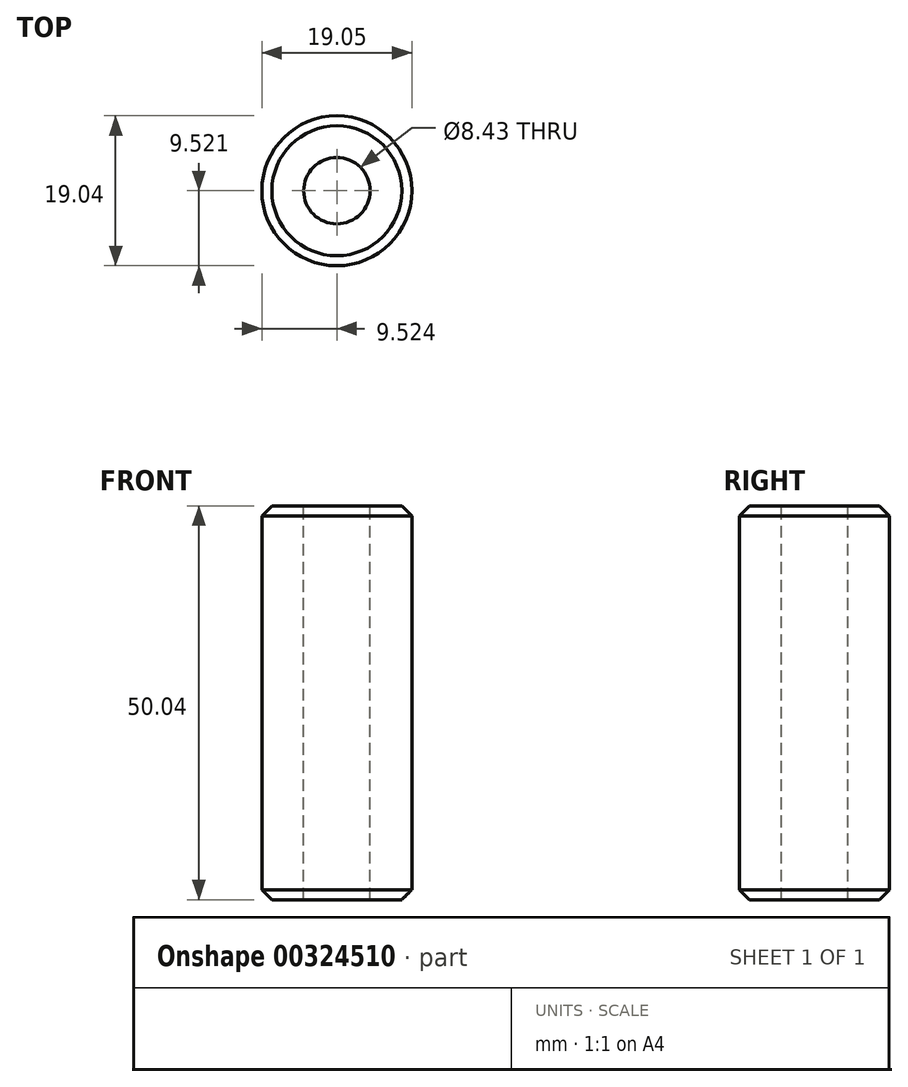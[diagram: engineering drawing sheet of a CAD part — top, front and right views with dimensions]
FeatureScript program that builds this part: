
annotation { "Feature Type Name" : "Feature", "Feature Type Description" : "" }
export const myFeature = defineFeature(function(context is Context, id is Id, definition is map)
    precondition{}
    {
        {
            var Q0;
            Q0=qCreatedBy(makeId("Top.planeOp"),FACE);
            var sketch = newSketch(context, id + "F0", { "sketchPlane" : qUnion([Q0])});
            skCircle(sketch, "E0", {"center": v(-11.47, 22.03) * mm, "radius": 9.52 * mm});
            skSolve(sketch);
        }
        {
            var Q0;
            Q0 = qSketchRegion(id + "F0", true);
            extrude(context, id + "F1", {"entities" : qUnion([Q0]), "depth" : 50.04 * mm});
        }
        {
            var Q0;
            Q0=makeQuery(id+"F1.opExtrude","CAP_FACE",FACE,{"disambiguationData":[OSD([sQuery(id+"F0.wireOp",EDGE,"E0")])],"isStart":false});
            var sketch = newSketch(context, id + "F2", { "sketchPlane" : qUnion([Q0])});
            skCircle(sketch, "E1", {"center": v(-11.47, 22.03) * mm, "radius": 4.21 * mm});
            skSolve(sketch);
        }
        {
            var Q0;
            Q0 = qSketchRegion(id + "F2", true);
            extrude(context, id + "F3", {"entities" : qUnion([Q0]), "operationType" : NewBodyOperationType.REMOVE, "oppositeDirection" : true, "depth" : 76.2 * mm});
        }
        {
            var Q0;
            Q0=makeQuery(id+"F1.opExtrude","CAP_EDGE",EDGE,{"disambiguationData":[OSD([sQuery(id+"F0.wireOp",EDGE,"E0")])],"isStart":true});
            var Q1;
            Q1=makeQuery(id+"F1.opExtrude","CAP_EDGE",EDGE,{"disambiguationData":[OSD([sQuery(id+"F0.wireOp",EDGE,"E0")])],"isStart":false});
            chamfer(context, id + "F4", {"entities" : qUnion([Q0, Q1]), "width" : 1.27 * mm, "tangentPropagation" : true});
        }
    });
